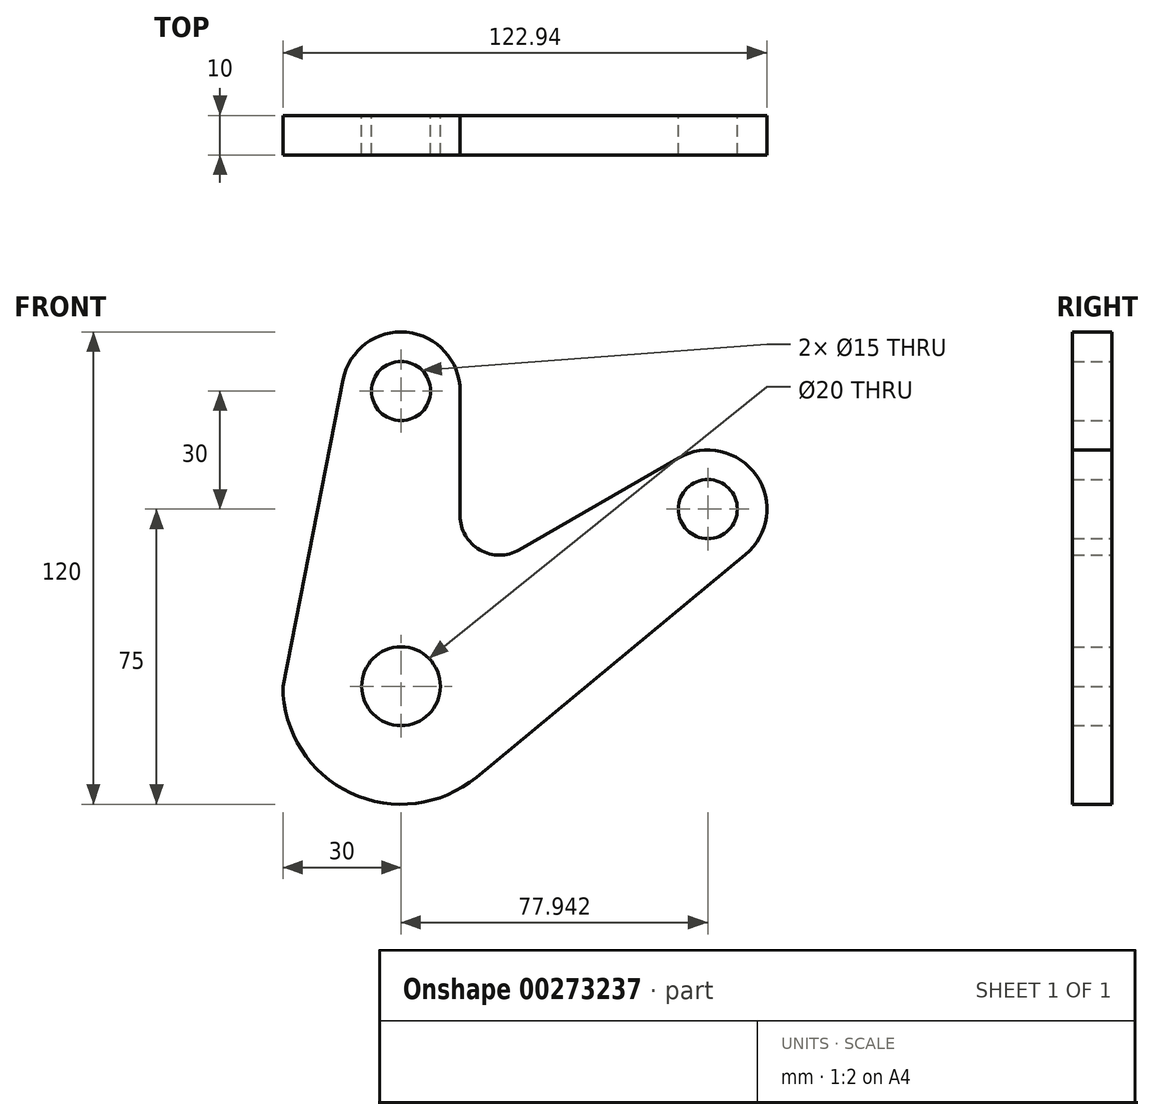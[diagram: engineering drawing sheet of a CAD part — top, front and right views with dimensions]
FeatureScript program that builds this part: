
annotation { "Feature Type Name" : "Feature", "Feature Type Description" : "" }
export const myFeature = defineFeature(function(context is Context, id is Id, definition is map)
    precondition{}
    {
        {
            var Q0;
            Q0=qCreatedBy(makeId("Front.planeOp"),FACE);
            var sketch = newSketch(context, id + "F0", { "sketchPlane" : qUnion([Q0])});
            skCircle(sketch, "E0", {"center": v(0, 0) * mm, "radius": 10 * mm});
            skCircle(sketch, "E1", {"center": v(0, 75) * mm, "radius": 7.5 * mm});
            skCircle(sketch, "E2", {"center": v(77.94, 45) * mm, "radius": 7.5 * mm});
            skLineSegment(sketch, "E3", {"start": v(-30, 0) * mm, "end": v(-14.72, 77.89) * mm});
            skLineSegment(sketch, "E4", {"start": v(19.12, -23.12) * mm, "end": v(87.5, 33.44) * mm});
            skArc(sketch, "E5", {"start": v(-30, 0) * mm, "mid": v(-12.77, -27.14) * mm, "end": v(19.12, -23.12) * mm});
            skLineSegment(sketch, "E6", {"start": v(70.44, 58) * mm, "end": v(30, 34.64) * mm});
            skLineSegment(sketch, "E7", {"start": v(15, 75) * mm, "end": v(15, 43.3) * mm});
            skArc(sketch, "E8", {"start": v(15, 75) * mm, "mid": v(1.45, 89.93) * mm, "end": v(-14.72, 77.89) * mm});
            skArc(sketch, "E9", {"start": v(15, 43.3) * mm, "mid": v(20, 34.64) * mm, "end": v(30, 34.64) * mm});
            skArc(sketch, "E10", {"start": v(87.5, 33.44) * mm, "mid": v(90.26, 53.56) * mm, "end": v(70.44, 58) * mm});
            skLineSegment(sketch, "E11", {"start": v(0, 75) * mm, "end": v(0, 0) * mm, "construction": true});
            skLineSegment(sketch, "E12", {"start": v(77.94, 45) * mm, "end": v(0, 0) * mm, "construction": true});
            skSolve(sketch);
        }
        {
            var Q0;
            Q0 = qSketchRegion(id + "F0", true);
            extrude(context, id + "F1", {"entities" : qUnion([Q0]), "depth" : 10 * mm});
        }
    });
